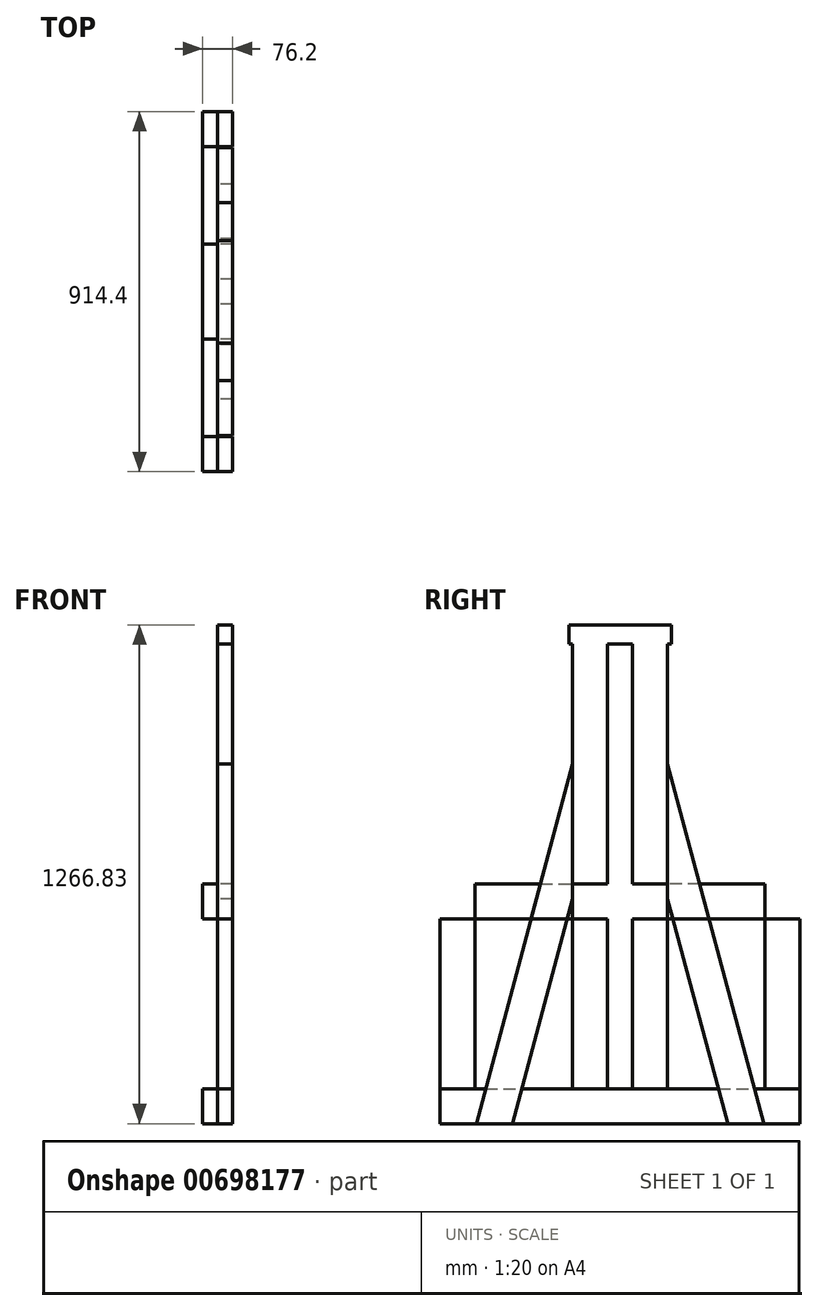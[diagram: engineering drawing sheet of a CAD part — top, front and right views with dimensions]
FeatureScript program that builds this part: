
annotation { "Feature Type Name" : "Feature", "Feature Type Description" : "" }
export const myFeature = defineFeature(function(context is Context, id is Id, definition is map)
    precondition{}
    {
        {
            var Q0;
            Q0=qCreatedBy(makeId("Right.planeOp"),FACE);
            var sketch = newSketch(context, id + "F0", { "sketchPlane" : qUnion([Q0])});
            skLineSegment(sketch, "E0.bottom", {"start": v(-457.2, 0) * mm, "end": v(457.2, 0) * mm});
            skLineSegment(sketch, "E0.top", {"start": v(-457.2, 88.9) * mm, "end": v(457.2, 88.9) * mm});
            skLineSegment(sketch, "E0.left", {"start": v(-457.2, 0) * mm, "end": v(-457.2, 88.9) * mm});
            skLineSegment(sketch, "E0.right", {"start": v(457.2, 0) * mm, "end": v(457.2, 88.9) * mm});
            skLineSegment(sketch, "E1.bottom", {"start": v(31.75, 0) * mm, "end": v(120.65, 0) * mm});
            skLineSegment(sketch, "E1.top", {"start": v(31.75, 1219.2) * mm, "end": v(120.65, 1219.2) * mm});
            skLineSegment(sketch, "E1.left", {"start": v(31.75, 0) * mm, "end": v(31.75, 1219.2) * mm});
            skLineSegment(sketch, "E1.right", {"start": v(120.65, 0) * mm, "end": v(120.65, 1219.2) * mm});
            skLineSegment(sketch, "E2", {"start": v(0, 0) * mm, "end": v(0, 1855.32) * mm, "construction": true});
            skLineSegment(sketch, "E3.bottom", {"start": v(-31.75, 0) * mm, "end": v(-120.65, 0) * mm});
            skLineSegment(sketch, "E3.top", {"start": v(-31.75, 1219.2) * mm, "end": v(-120.65, 1219.2) * mm});
            skLineSegment(sketch, "E3.left", {"start": v(-31.75, 0) * mm, "end": v(-31.75, 1219.2) * mm});
            skLineSegment(sketch, "E3.right", {"start": v(-120.65, 0) * mm, "end": v(-120.65, 1219.2) * mm});
            skLineSegment(sketch, "E4.bottom", {"start": v(-457.2, 0) * mm, "end": v(-368.3, 0) * mm});
            skLineSegment(sketch, "E4.top", {"start": v(-457.2, 609.6) * mm, "end": v(-368.3, 609.6) * mm});
            skLineSegment(sketch, "E4.left", {"start": v(-457.2, 0) * mm, "end": v(-457.2, 609.6) * mm});
            skLineSegment(sketch, "E4.right", {"start": v(-368.3, 0) * mm, "end": v(-368.3, 609.6) * mm});
            skLineSegment(sketch, "E5.bottom", {"start": v(457.2, 0) * mm, "end": v(368.3, 0) * mm});
            skLineSegment(sketch, "E5.top", {"start": v(457.2, 609.6) * mm, "end": v(368.3, 609.6) * mm});
            skLineSegment(sketch, "E5.left", {"start": v(457.2, 0) * mm, "end": v(457.2, 609.6) * mm});
            skLineSegment(sketch, "E5.right", {"start": v(368.3, 0) * mm, "end": v(368.3, 609.6) * mm});
            skLineSegment(sketch, "E6.bottom", {"start": v(-457.2, 609.6) * mm, "end": v(-31.75, 609.6) * mm});
            skLineSegment(sketch, "E6.top", {"start": v(-457.2, 520.7) * mm, "end": v(-31.75, 520.7) * mm});
            skLineSegment(sketch, "E6.left", {"start": v(-457.2, 609.6) * mm, "end": v(-457.2, 520.7) * mm});
            skLineSegment(sketch, "E6.right", {"start": v(-31.75, 609.6) * mm, "end": v(-31.75, 520.7) * mm});
            skLineSegment(sketch, "E7.bottom", {"start": v(457.2, 609.6) * mm, "end": v(31.75, 609.6) * mm});
            skLineSegment(sketch, "E7.top", {"start": v(457.2, 520.7) * mm, "end": v(31.75, 520.7) * mm});
            skLineSegment(sketch, "E7.left", {"start": v(457.2, 609.6) * mm, "end": v(457.2, 520.7) * mm});
            skLineSegment(sketch, "E7.right", {"start": v(31.75, 609.6) * mm, "end": v(31.75, 520.7) * mm});
            skLineSegment(sketch, "E8", {"start": v(-365.84, -0.66) * mm, "end": v(-120.65, 914.4) * mm});
            skLineSegment(sketch, "E9", {"start": v(-120.65, 570.92) * mm, "end": v(-273.63, 0) * mm});
            skLineSegment(sketch, "E10.MirrorCS", {"start": v(365.84, -0.66) * mm, "end": v(120.65, 914.4) * mm});
            skLineSegment(sketch, "E11.MirrorCS", {"start": v(120.65, 570.92) * mm, "end": v(273.63, 0) * mm});
            skLineSegment(sketch, "E12", {"start": v(-120.65, 914.4) * mm, "end": v(-120.65, 570.92) * mm});
            skLineSegment(sketch, "E13", {"start": v(-365.84, -0.66) * mm, "end": v(-273.63, 0) * mm});
            skLineSegment(sketch, "E14", {"start": v(120.65, 570.92) * mm, "end": v(120.65, 914.4) * mm});
            skLineSegment(sketch, "E15", {"start": v(-120.65, 570.92) * mm, "end": v(-120.65, 914.4) * mm});
            skLineSegment(sketch, "E16.MirrorCS", {"start": v(120.65, 914.4) * mm, "end": v(120.65, 570.92) * mm});
            skLineSegment(sketch, "E17.bottom", {"start": v(-130.2, 1219.2) * mm, "end": v(130.15, 1219.2) * mm});
            skLineSegment(sketch, "E17.top", {"start": v(-130.2, 1266.83) * mm, "end": v(130.15, 1266.83) * mm});
            skLineSegment(sketch, "E17.left", {"start": v(-130.2, 1219.2) * mm, "end": v(-130.2, 1266.83) * mm});
            skLineSegment(sketch, "E17.right", {"start": v(130.15, 1219.2) * mm, "end": v(130.15, 1266.83) * mm});
            skSolve(sketch);
        }
        {
            var Q0;
            {var subQ0=sQuery(id+"F0.wireOp",EDGE,"E0.right");Q0=makeQuery(id+"F0.imprint","IMPRINT",FACE,{"disambiguationData":[TD([[makeQuery(id+"F0.imprint","IMPRINT",EDGE,{"derivedFrom":subQ0}),1.0]])]});}
            var Q1;
            {var subQ0=sQuery(id+"F0.wireOp",EDGE,"O3M96ZiU-TQwq-dLFp-mwfa-ZtAqAqBcbGVx.right");var subQ5=sQuery(id+"F0.wireOp",EDGE,"E0.top");var subQ6=makeQuery(id+"F0.imprint","INTERSECT",VERTEX,{"derivedFrom":[subQ5,subQ0]});Q1=makeQuery(id+"F0.imprint","IMPRINT",FACE,{"disambiguationData":[TD([[makeQuery(id+"F0.imprint","IMPRINT",EDGE,{"disambiguationData":[TD([[subQ6,-1.0]])],"derivedFrom":subQ5}),-1.0]])]});}
            var Q2;
            {var subQ0=sQuery(id+"F0.wireOp",EDGE,"E0.left");Q2=makeQuery(id+"F0.imprint","IMPRINT",FACE,{"disambiguationData":[TD([[makeQuery(id+"F0.imprint","IMPRINT",EDGE,{"derivedFrom":subQ0}),-1.0]])]});}
            var Q3;
            {var subQ5=sQuery(id+"F0.wireOp",EDGE,"O3M96ZiU-TQwq-dLFp-mwfa-ZtAqAqBcbGVx.bottom");Q3=makeQuery(id+"F0.imprint","IMPRINT",FACE,{"disambiguationData":[TD([[makeQuery(id+"F0.imprint","IMPRINT",EDGE,{"derivedFrom":subQ5}),1.0]])]});}
            var Q4;
            {var subQ5=sQuery(id+"F0.wireOp",EDGE,"E1.bottom");Q4=makeQuery(id+"F0.imprint","IMPRINT",FACE,{"disambiguationData":[TD([[makeQuery(id+"F0.imprint","IMPRINT",EDGE,{"derivedFrom":subQ5}),1.0]])]});}
            var Q5;
            {var subQ0=sQuery(id+"F0.wireOp",EDGE,"E6.bottom");var subQ1=sQuery(id+"F0.wireOp",EDGE,"E4.right");var subQ2=makeQuery(id+"F0.imprint","INTERSECT",VERTEX,{"derivedFrom":[subQ1,subQ0]});Q5=makeQuery(id+"F0.imprint","IMPRINT",FACE,{"disambiguationData":[TD([[makeQuery(id+"F0.imprint","IMPRINT",EDGE,{"disambiguationData":[TD([[subQ2,1.0]])],"derivedFrom":subQ1}),-1.0]])]});}
            var Q6;
            {var subQ5=sQuery(id+"F0.wireOp",EDGE,"E3.right");var subQ7=sQuery(id+"F0.wireOp",EDGE,"E9");var subQ9=makeQuery(id+"F0.imprint","INTERSECT",VERTEX,{"derivedFrom":[subQ5,subQ7]});Q6=makeQuery(id+"F0.imprint","IMPRINT",FACE,{"disambiguationData":[TD([[makeQuery(id+"F0.imprint","IMPRINT",EDGE,{"disambiguationData":[TD([[subQ9,-1.0]])],"derivedFrom":subQ5}),1.0]])]});}
            var Q7;
            {var subQ0=sQuery(id+"F0.wireOp",EDGE,"E9");var subQ1=sQuery(id+"F0.wireOp",EDGE,"E3.right");var subQ2=makeQuery(id+"F0.imprint","INTERSECT",VERTEX,{"derivedFrom":[subQ1,subQ0]});Q7=makeQuery(id+"F0.imprint","IMPRINT",FACE,{"disambiguationData":[TD([[makeQuery(id+"F0.imprint","IMPRINT",EDGE,{"disambiguationData":[TD([[subQ2,1.0]])],"derivedFrom":subQ1}),1.0]])]});}
            var Q8;
            {var subQ0=sQuery(id+"F0.wireOp",EDGE,"E6.right");Q8=makeQuery(id+"F0.imprint","IMPRINT",FACE,{"disambiguationData":[TD([[makeQuery(id+"F0.imprint","IMPRINT",EDGE,{"derivedFrom":subQ0}),-1.0]])]});}
            var Q9;
            {var subQ5=sQuery(id+"F0.wireOp",EDGE,"E6.left");Q9=makeQuery(id+"F0.imprint","IMPRINT",FACE,{"disambiguationData":[TD([[makeQuery(id+"F0.imprint","IMPRINT",EDGE,{"derivedFrom":subQ5}),1.0]])]});}
            var Q10;
            {var subQ0=sQuery(id+"F0.wireOp",EDGE,"E7.right");Q10=makeQuery(id+"F0.imprint","IMPRINT",FACE,{"disambiguationData":[TD([[makeQuery(id+"F0.imprint","IMPRINT",EDGE,{"derivedFrom":subQ0}),1.0]])]});}
            var Q11;
            {var subQ0=sQuery(id+"F0.wireOp",EDGE,"E11.MirrorCS");var subQ1=sQuery(id+"F0.wireOp",EDGE,"E1.right");var subQ2=makeQuery(id+"F0.imprint","INTERSECT",VERTEX,{"derivedFrom":[subQ1,subQ0]});Q11=makeQuery(id+"F0.imprint","IMPRINT",FACE,{"disambiguationData":[TD([[makeQuery(id+"F0.imprint","IMPRINT",EDGE,{"disambiguationData":[TD([[subQ2,1.0]])],"derivedFrom":subQ1}),-1.0]])]});}
            var Q12;
            {var subQ5=sQuery(id+"F0.wireOp",EDGE,"E11.MirrorCS");var subQ7=sQuery(id+"F0.wireOp",EDGE,"E1.right");var subQ9=makeQuery(id+"F0.imprint","INTERSECT",VERTEX,{"derivedFrom":[subQ7,subQ5]});Q12=makeQuery(id+"F0.imprint","IMPRINT",FACE,{"disambiguationData":[TD([[makeQuery(id+"F0.imprint","IMPRINT",EDGE,{"disambiguationData":[TD([[subQ9,-1.0]])],"derivedFrom":subQ7}),-1.0]])]});}
            var Q13;
            {var subQ0=sQuery(id+"F0.wireOp",EDGE,"E7.bottom");var subQ1=sQuery(id+"F0.wireOp",EDGE,"E5.right");var subQ2=makeQuery(id+"F0.imprint","INTERSECT",VERTEX,{"derivedFrom":[subQ1,subQ0]});Q13=makeQuery(id+"F0.imprint","IMPRINT",FACE,{"disambiguationData":[TD([[makeQuery(id+"F0.imprint","IMPRINT",EDGE,{"disambiguationData":[TD([[subQ2,1.0]])],"derivedFrom":subQ1}),1.0]])]});}
            var Q14;
            {var subQ5=sQuery(id+"F0.wireOp",EDGE,"E7.left");Q14=makeQuery(id+"F0.imprint","IMPRINT",FACE,{"disambiguationData":[TD([[makeQuery(id+"F0.imprint","IMPRINT",EDGE,{"derivedFrom":subQ5}),-1.0]])]});}
            var Q15;
            {var subQ0=sQuery(id+"F0.wireOp",EDGE,"E8");var subQ1=sQuery(id+"F0.wireOp",EDGE,"E6.bottom");var subQ2=makeQuery(id+"F0.imprint","INTERSECT",VERTEX,{"derivedFrom":[subQ1,subQ0]});Q15=makeQuery(id+"F0.imprint","IMPRINT",FACE,{"disambiguationData":[TD([[makeQuery(id+"F0.imprint","IMPRINT",EDGE,{"disambiguationData":[TD([[subQ2,-1.0]])],"derivedFrom":subQ1}),-1.0]])]});}
            var Q16;
            {var subQ5=sQuery(id+"F0.wireOp",EDGE,"E10.MirrorCS");var subQ6=sQuery(id+"F0.wireOp",EDGE,"E7.bottom");var subQ7=makeQuery(id+"F0.imprint","INTERSECT",VERTEX,{"derivedFrom":[subQ6,subQ5]});Q16=makeQuery(id+"F0.imprint","IMPRINT",FACE,{"disambiguationData":[TD([[makeQuery(id+"F0.imprint","IMPRINT",EDGE,{"disambiguationData":[TD([[subQ7,-1.0]])],"derivedFrom":subQ6}),1.0]])]});}
            extrude(context, id + "F1", {"entities" : qUnion([Q0, Q1, Q2, Q3, Q4, Q5, Q6, Q7, Q8, Q9, Q10, Q11, Q12, Q13, Q14, Q15, Q16]), "oppositeDirection" : true, "depth" : 38.1 * mm, "offsetDistance" : 25.4 * mm});
        }
        {
            var Q0;
            {var subQ5=sQuery(id+"F0.wireOp",EDGE,"E3.top");Q0=makeQuery(id+"F0.imprint","IMPRINT",FACE,{"disambiguationData":[TD([[makeQuery(id+"F0.imprint","IMPRINT",EDGE,{"derivedFrom":subQ5}),1.0]])]});}
            var Q1;
            {var subQ5=sQuery(id+"F0.wireOp",EDGE,"E1.top");Q1=makeQuery(id+"F0.imprint","IMPRINT",FACE,{"disambiguationData":[TD([[makeQuery(id+"F0.imprint","IMPRINT",EDGE,{"derivedFrom":subQ5}),-1.0]])]});}
            var Q2;
            {var subQ5=sQuery(id+"F0.wireOp",EDGE,"E3.bottom");Q2=makeQuery(id+"F0.imprint","IMPRINT",FACE,{"disambiguationData":[TD([[makeQuery(id+"F0.imprint","IMPRINT",EDGE,{"derivedFrom":subQ5}),-1.0]])]});}
            var Q3;
            {var subQ5=sQuery(id+"F0.wireOp",EDGE,"E1.bottom");Q3=makeQuery(id+"F0.imprint","IMPRINT",FACE,{"disambiguationData":[TD([[makeQuery(id+"F0.imprint","IMPRINT",EDGE,{"derivedFrom":subQ5}),1.0]])]});}
            var Q4;
            {var subQ0=sQuery(id+"F0.wireOp",EDGE,"E6.right");Q4=makeQuery(id+"F0.imprint","IMPRINT",FACE,{"disambiguationData":[TD([[makeQuery(id+"F0.imprint","IMPRINT",EDGE,{"derivedFrom":subQ0}),-1.0]])]});}
            var Q5;
            {var subQ0=sQuery(id+"F0.wireOp",EDGE,"E3.left");var subQ1=sQuery(id+"F0.wireOp",EDGE,"E0.top");var subQ2=makeQuery(id+"F0.imprint","INTERSECT",VERTEX,{"derivedFrom":[subQ1,subQ0]});Q5=makeQuery(id+"F0.imprint","IMPRINT",FACE,{"disambiguationData":[TD([[makeQuery(id+"F0.imprint","IMPRINT",EDGE,{"disambiguationData":[TD([[subQ2,1.0]])],"derivedFrom":subQ1}),1.0]])]});}
            var Q6;
            {var subQ0=sQuery(id+"F0.wireOp",EDGE,"E1.left");var subQ1=sQuery(id+"F0.wireOp",EDGE,"E0.top");var subQ2=makeQuery(id+"F0.imprint","INTERSECT",VERTEX,{"derivedFrom":[subQ1,subQ0]});Q6=makeQuery(id+"F0.imprint","IMPRINT",FACE,{"disambiguationData":[TD([[makeQuery(id+"F0.imprint","IMPRINT",EDGE,{"disambiguationData":[TD([[subQ2,-1.0]])],"derivedFrom":subQ1}),1.0]])]});}
            var Q7;
            {var subQ0=sQuery(id+"F0.wireOp",EDGE,"E7.right");Q7=makeQuery(id+"F0.imprint","IMPRINT",FACE,{"disambiguationData":[TD([[makeQuery(id+"F0.imprint","IMPRINT",EDGE,{"derivedFrom":subQ0}),1.0]])]});}
            var Q8;
            {var subQ0=sQuery(id+"F0.wireOp",EDGE,"E4.left");var subQ1=sQuery(id+"F0.wireOp",EDGE,"E0.top");var subQ2=makeQuery(id+"F0.imprint","INTERSECT",VERTEX,{"derivedFrom":[subQ1,subQ0]});Q8=makeQuery(id+"F0.imprint","IMPRINT",FACE,{"disambiguationData":[TD([[makeQuery(id+"F0.imprint","IMPRINT",EDGE,{"disambiguationData":[TD([[subQ2,-1.0]])],"derivedFrom":subQ1}),1.0]])]});}
            var Q9;
            {var subQ5=sQuery(id+"F0.wireOp",EDGE,"E6.left");Q9=makeQuery(id+"F0.imprint","IMPRINT",FACE,{"disambiguationData":[TD([[makeQuery(id+"F0.imprint","IMPRINT",EDGE,{"derivedFrom":subQ5}),1.0]])]});}
            var Q10;
            {var subQ5=sQuery(id+"F0.wireOp",EDGE,"E4.bottom");Q10=makeQuery(id+"F0.imprint","IMPRINT",FACE,{"disambiguationData":[TD([[makeQuery(id+"F0.imprint","IMPRINT",EDGE,{"derivedFrom":subQ5}),1.0]])]});}
            var Q11;
            {var subQ5=sQuery(id+"F0.wireOp",EDGE,"E7.left");Q11=makeQuery(id+"F0.imprint","IMPRINT",FACE,{"disambiguationData":[TD([[makeQuery(id+"F0.imprint","IMPRINT",EDGE,{"derivedFrom":subQ5}),-1.0]])]});}
            var Q12;
            {var subQ0=sQuery(id+"F0.wireOp",EDGE,"E5.left");var subQ1=sQuery(id+"F0.wireOp",EDGE,"E0.top");var subQ2=makeQuery(id+"F0.imprint","INTERSECT",VERTEX,{"derivedFrom":[subQ1,subQ0]});Q12=makeQuery(id+"F0.imprint","IMPRINT",FACE,{"disambiguationData":[TD([[makeQuery(id+"F0.imprint","IMPRINT",EDGE,{"disambiguationData":[TD([[subQ2,1.0]])],"derivedFrom":subQ1}),1.0]])]});}
            var Q13;
            {var subQ5=sQuery(id+"F0.wireOp",EDGE,"E5.bottom");Q13=makeQuery(id+"F0.imprint","IMPRINT",FACE,{"disambiguationData":[TD([[makeQuery(id+"F0.imprint","IMPRINT",EDGE,{"derivedFrom":subQ5}),-1.0]])]});}
            var Q14;
            {var subQ0=sQuery(id+"F0.wireOp",EDGE,"E8");var subQ1=sQuery(id+"F0.wireOp",EDGE,"E3.right");var subQ2=makeQuery(id+"F0.imprint","INTERSECT",VERTEX,{"derivedFrom":[subQ1,subQ0]});Q14=makeQuery(id+"F0.imprint","IMPRINT",FACE,{"disambiguationData":[TD([[makeQuery(id+"F0.imprint","IMPRINT",EDGE,{"disambiguationData":[TD([[subQ2,1.0]])],"derivedFrom":subQ1}),1.0]])]});}
            var Q15;
            {var subQ5=sQuery(id+"F0.wireOp",EDGE,"E3.right");var subQ7=sQuery(id+"F0.wireOp",EDGE,"E9");var subQ9=makeQuery(id+"F0.imprint","INTERSECT",VERTEX,{"derivedFrom":[subQ5,subQ7]});Q15=makeQuery(id+"F0.imprint","IMPRINT",FACE,{"disambiguationData":[TD([[makeQuery(id+"F0.imprint","IMPRINT",EDGE,{"disambiguationData":[TD([[subQ9,-1.0]])],"derivedFrom":subQ5}),1.0]])]});}
            var Q16;
            {var subQ0=sQuery(id+"F0.wireOp",EDGE,"E10.MirrorCS");var subQ1=sQuery(id+"F0.wireOp",EDGE,"E1.right");var subQ2=makeQuery(id+"F0.imprint","INTERSECT",VERTEX,{"derivedFrom":[subQ1,subQ0]});Q16=makeQuery(id+"F0.imprint","IMPRINT",FACE,{"disambiguationData":[TD([[makeQuery(id+"F0.imprint","IMPRINT",EDGE,{"disambiguationData":[TD([[subQ2,1.0]])],"derivedFrom":subQ1}),-1.0]])]});}
            var Q17;
            {var subQ5=sQuery(id+"F0.wireOp",EDGE,"E11.MirrorCS");var subQ7=sQuery(id+"F0.wireOp",EDGE,"E1.right");var subQ9=makeQuery(id+"F0.imprint","INTERSECT",VERTEX,{"derivedFrom":[subQ7,subQ5]});Q17=makeQuery(id+"F0.imprint","IMPRINT",FACE,{"disambiguationData":[TD([[makeQuery(id+"F0.imprint","IMPRINT",EDGE,{"disambiguationData":[TD([[subQ9,-1.0]])],"derivedFrom":subQ7}),-1.0]])]});}
            var Q18;
            {var subQ5=sQuery(id+"F0.wireOp",EDGE,"E17.bottom");var subQ7=sQuery(id+"F0.wireOp",EDGE,"E3.left");var subQ9=makeQuery(id+"F0.imprint","INTERSECT",VERTEX,{"derivedFrom":[subQ7,subQ5]});Q18=makeQuery(id+"F0.imprint","IMPRINT",FACE,{"disambiguationData":[TD([[makeQuery(id+"F0.imprint","IMPRINT",EDGE,{"disambiguationData":[TD([[subQ9,1.0]])],"derivedFrom":subQ5}),-1.0]])]});}
            var Q19;
            {var subQ1=sQuery(id+"F0.wireOp",EDGE,"E1.left");var subQ5=sQuery(id+"F0.wireOp",EDGE,"E17.bottom");var subQ9=makeQuery(id+"F0.imprint","INTERSECT",VERTEX,{"derivedFrom":[subQ1,subQ5]});Q19=makeQuery(id+"F0.imprint","IMPRINT",FACE,{"disambiguationData":[TD([[makeQuery(id+"F0.imprint","IMPRINT",EDGE,{"disambiguationData":[TD([[subQ9,-1.0]])],"derivedFrom":subQ5}),-1.0]])]});}
            var Q20;
            Q20=makeQuery(id+"F0.imprint","IMPRINT",FACE,{"disambiguationData":[TD([[makeQuery(id+"F0.imprint","IMPRINT",EDGE,{"derivedFrom":sQuery(id+"F0.wireOp",EDGE,"E17.top")}),-1.0]])]});
            var Q21;
            {var subQ5=sQuery(id+"F0.wireOp",EDGE,"E17.bottom");var subQ7=sQuery(id+"F0.wireOp",EDGE,"E3.left");var subQ9=makeQuery(id+"F0.imprint","INTERSECT",VERTEX,{"derivedFrom":[subQ7,subQ5]});Q21=makeQuery(id+"F0.imprint","IMPRINT",FACE,{"disambiguationData":[TD([[makeQuery(id+"F0.imprint","IMPRINT",EDGE,{"disambiguationData":[TD([[subQ9,1.0]])],"derivedFrom":subQ5}),-1.0]])]});}
            var Q22;
            {var subQ1=sQuery(id+"F0.wireOp",EDGE,"E1.left");var subQ5=sQuery(id+"F0.wireOp",EDGE,"E17.bottom");var subQ9=makeQuery(id+"F0.imprint","INTERSECT",VERTEX,{"derivedFrom":[subQ1,subQ5]});Q22=makeQuery(id+"F0.imprint","IMPRINT",FACE,{"disambiguationData":[TD([[makeQuery(id+"F0.imprint","IMPRINT",EDGE,{"disambiguationData":[TD([[subQ9,-1.0]])],"derivedFrom":subQ5}),-1.0]])]});}
            extrude(context, id + "F2", {"entities" : qUnion([Q0, Q1, Q2, Q3, Q4, Q5, Q6, Q7, Q8, Q9, Q10, Q11, Q12, Q13, Q14, Q15, Q16, Q17, Q18, Q19, Q20, Q21, Q22]), "depth" : 38.1 * mm, "offsetDistance" : 25.4 * mm});
        }
        {
            var Q0;
            {var subQ0=sQuery(id+"F0.wireOp",EDGE,"E8");var subQ1=sQuery(id+"F0.wireOp",EDGE,"E6.bottom");var subQ2=makeQuery(id+"F0.imprint","INTERSECT",VERTEX,{"derivedFrom":[subQ1,subQ0]});Q0=makeQuery(id+"F0.imprint","IMPRINT",FACE,{"disambiguationData":[TD([[makeQuery(id+"F0.imprint","IMPRINT",EDGE,{"disambiguationData":[TD([[subQ2,-1.0]])],"derivedFrom":subQ1}),1.0]])]});}
            var Q1;
            {var subQ0=sQuery(id+"F0.wireOp",EDGE,"E8");var subQ1=sQuery(id+"F0.wireOp",EDGE,"E6.bottom");var subQ2=makeQuery(id+"F0.imprint","INTERSECT",VERTEX,{"derivedFrom":[subQ1,subQ0]});Q1=makeQuery(id+"F0.imprint","IMPRINT",FACE,{"disambiguationData":[TD([[makeQuery(id+"F0.imprint","IMPRINT",EDGE,{"disambiguationData":[TD([[subQ2,-1.0]])],"derivedFrom":subQ1}),-1.0]])]});}
            var Q2;
            {var subQ0=sQuery(id+"F0.wireOp",EDGE,"E8");var subQ1=sQuery(id+"F0.wireOp",EDGE,"E0.top");var subQ2=makeQuery(id+"F0.imprint","INTERSECT",VERTEX,{"derivedFrom":[subQ1,subQ0]});Q2=makeQuery(id+"F0.imprint","IMPRINT",FACE,{"disambiguationData":[TD([[makeQuery(id+"F0.imprint","IMPRINT",EDGE,{"disambiguationData":[TD([[subQ2,-1.0]])],"derivedFrom":subQ1}),1.0]])]});}
            var Q3;
            {var subQ0=sQuery(id+"F0.wireOp",EDGE,"E10.MirrorCS");var subQ1=sQuery(id+"F0.wireOp",EDGE,"E7.bottom");var subQ2=makeQuery(id+"F0.imprint","INTERSECT",VERTEX,{"derivedFrom":[subQ1,subQ0]});Q3=makeQuery(id+"F0.imprint","IMPRINT",FACE,{"disambiguationData":[TD([[makeQuery(id+"F0.imprint","IMPRINT",EDGE,{"disambiguationData":[TD([[subQ2,-1.0]])],"derivedFrom":subQ1}),-1.0]])]});}
            var Q4;
            {var subQ5=sQuery(id+"F0.wireOp",EDGE,"E10.MirrorCS");var subQ6=sQuery(id+"F0.wireOp",EDGE,"E7.bottom");var subQ7=makeQuery(id+"F0.imprint","INTERSECT",VERTEX,{"derivedFrom":[subQ6,subQ5]});Q4=makeQuery(id+"F0.imprint","IMPRINT",FACE,{"disambiguationData":[TD([[makeQuery(id+"F0.imprint","IMPRINT",EDGE,{"disambiguationData":[TD([[subQ7,-1.0]])],"derivedFrom":subQ6}),1.0]])]});}
            var Q5;
            {var subQ0=sQuery(id+"F0.wireOp",EDGE,"E11.MirrorCS");var subQ1=sQuery(id+"F0.wireOp",EDGE,"E0.top");var subQ2=makeQuery(id+"F0.imprint","INTERSECT",VERTEX,{"derivedFrom":[subQ1,subQ0]});Q5=makeQuery(id+"F0.imprint","IMPRINT",FACE,{"disambiguationData":[TD([[makeQuery(id+"F0.imprint","IMPRINT",EDGE,{"disambiguationData":[TD([[subQ2,-1.0]])],"derivedFrom":subQ1}),1.0]])]});}
            var Q6;
            {var subQ3=sQuery(id+"F0.wireOp",EDGE,"E8");var subQ5=sQuery(id+"F0.wireOp",EDGE,"E0.top");var subQ6=makeQuery(id+"F0.imprint","INTERSECT",VERTEX,{"derivedFrom":[subQ5,subQ3]});Q6=makeQuery(id+"F0.imprint","IMPRINT",FACE,{"disambiguationData":[TD([[makeQuery(id+"F0.imprint","IMPRINT",EDGE,{"disambiguationData":[TD([[subQ6,-1.0]])],"derivedFrom":subQ5}),-1.0]])]});}
            var Q7;
            {var subQ0=sQuery(id+"F0.wireOp",EDGE,"E11.MirrorCS");var subQ1=sQuery(id+"F0.wireOp",EDGE,"E0.bottom");var subQ2=makeQuery(id+"F0.imprint","INTERSECT",VERTEX,{"derivedFrom":[subQ1,subQ0]});Q7=makeQuery(id+"F0.imprint","IMPRINT",FACE,{"disambiguationData":[TD([[makeQuery(id+"F0.imprint","IMPRINT",EDGE,{"disambiguationData":[TD([[subQ2,-1.0]])],"derivedFrom":subQ1}),1.0]])]});}
            extrude(context, id + "F3", {"entities" : qUnion([Q0, Q1, Q2, Q3, Q4, Q5, Q6, Q7]), "depth" : 38.1 * mm, "offsetDistance" : 25.4 * mm});
        }
    });
